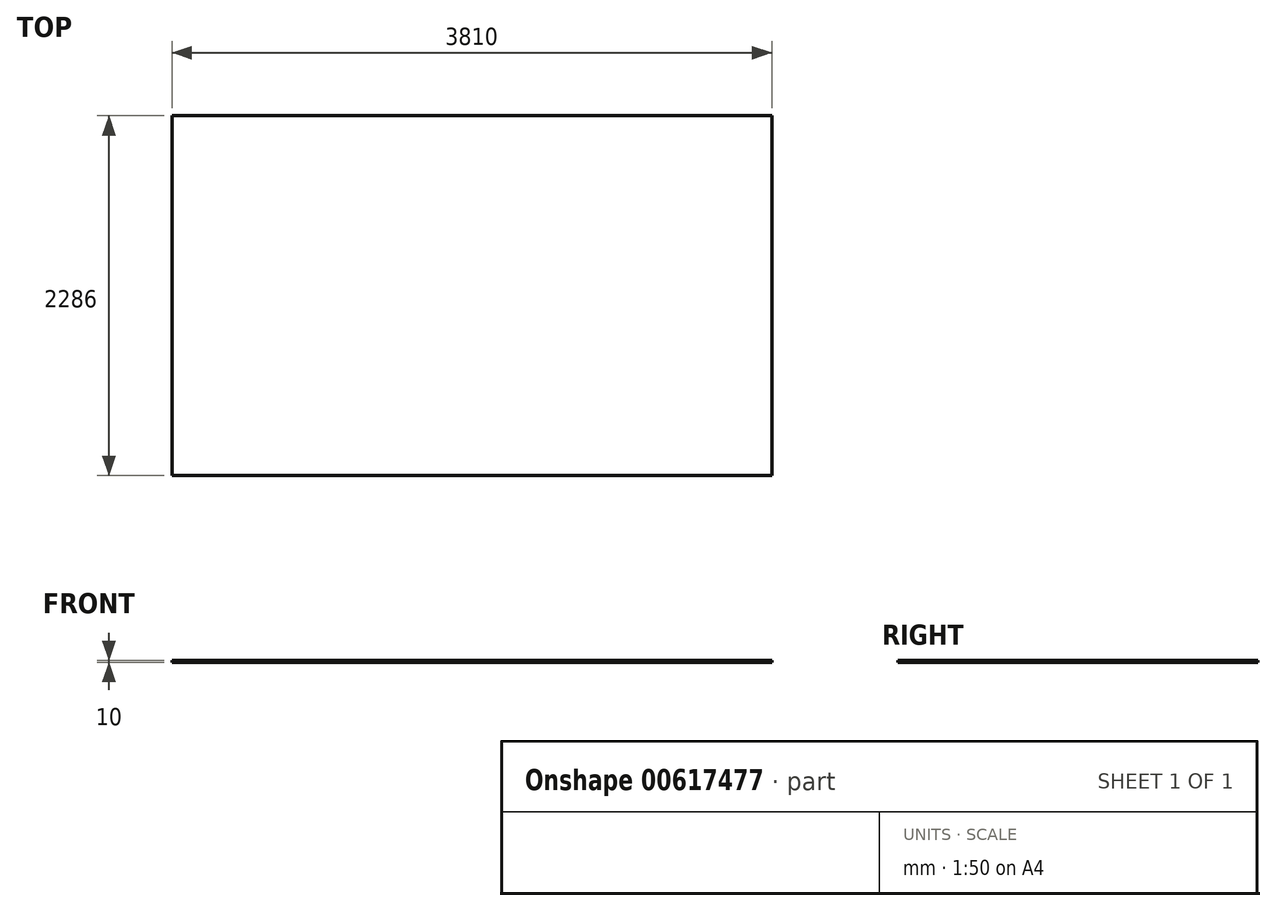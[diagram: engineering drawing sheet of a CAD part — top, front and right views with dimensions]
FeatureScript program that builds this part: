
annotation { "Feature Type Name" : "Feature", "Feature Type Description" : "" }
export const myFeature = defineFeature(function(context is Context, id is Id, definition is map)
    precondition{}
    {
        {
            var Q0;
            Q0=qCreatedBy(makeId("Top.planeOp"),FACE);
            var sketch = newSketch(context, id + "F0", { "sketchPlane" : qUnion([Q0])});
            skLineSegment(sketch, "E0.bottom", {"start": v(-1905, 1143) * mm, "end": v(1905, 1143) * mm});
            skLineSegment(sketch, "E0.top", {"start": v(-1905, -1143) * mm, "end": v(1905, -1143) * mm});
            skLineSegment(sketch, "E0.left", {"start": v(-1905, 1143) * mm, "end": v(-1905, -1143) * mm});
            skLineSegment(sketch, "E0.right", {"start": v(1905, 1143) * mm, "end": v(1905, -1143) * mm});
            skPoint(sketch, "E0.middle", {"position": v(0, 0) * mm});
            skSolve(sketch);
        }
        {
            var Q0;
            Q0 = qSketchRegion(id + "F0", true);
            extrude(context, id + "F1", {"entities" : qUnion([Q0]), "depth" : 10 * mm, "offsetDistance" : 25.4 * mm});
        }
    });
